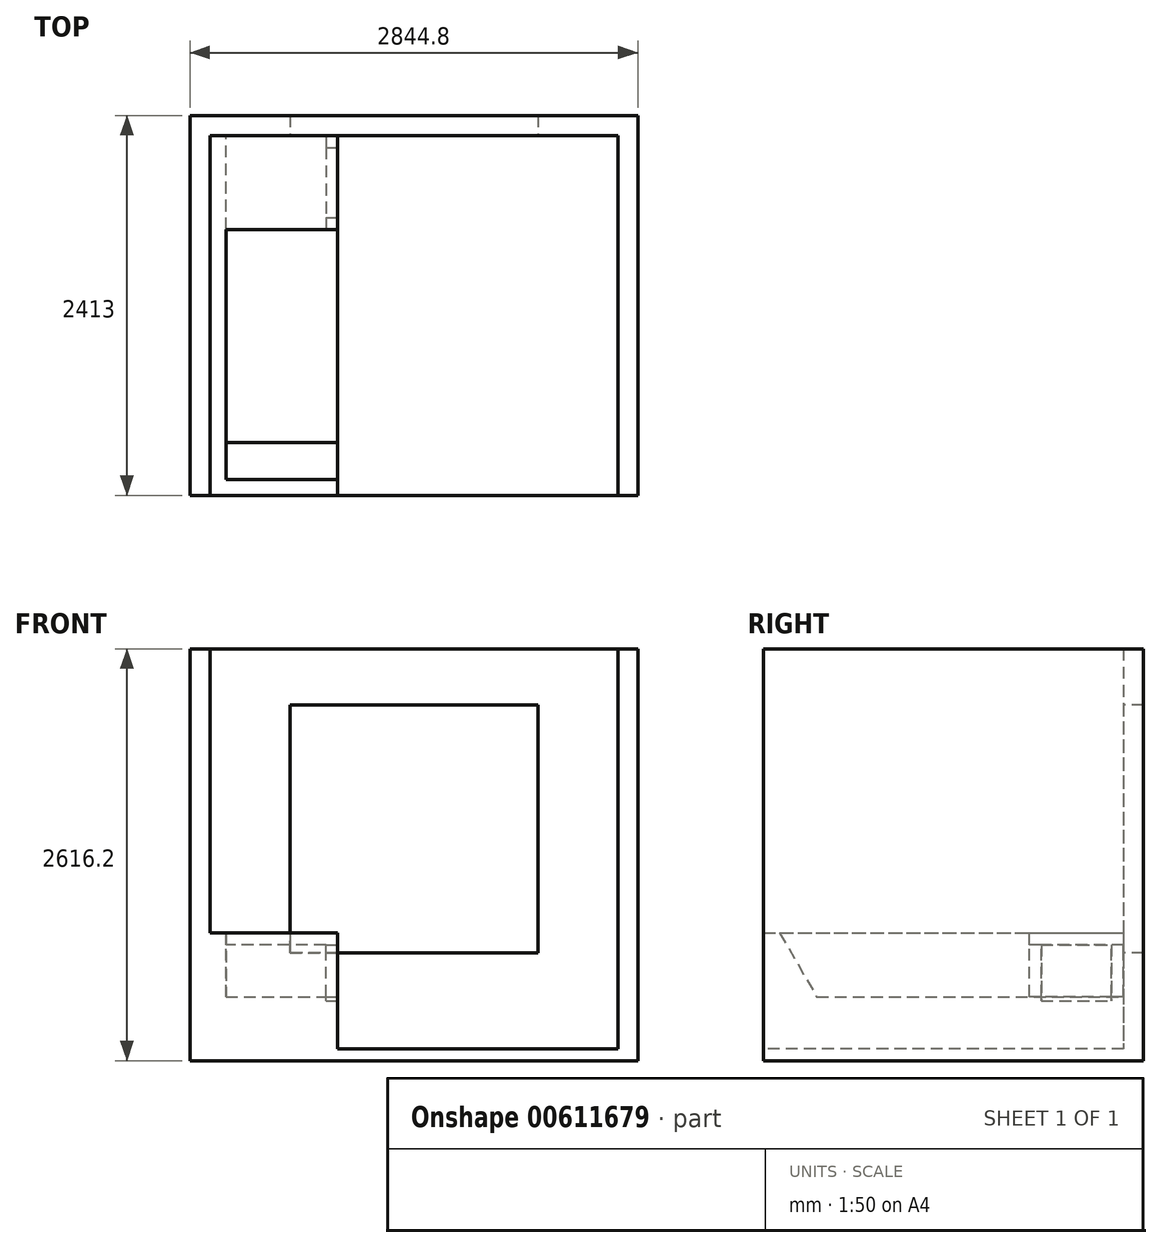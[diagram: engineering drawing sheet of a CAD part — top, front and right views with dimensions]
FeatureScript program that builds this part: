
annotation { "Feature Type Name" : "Feature", "Feature Type Description" : "" }
export const myFeature = defineFeature(function(context is Context, id is Id, definition is map)
    precondition{}
    {
        {
            var Q0;
            Q0=qCreatedBy(makeId("Top.planeOp"),FACE);
            var sketch = newSketch(context, id + "F0", { "sketchPlane" : qUnion([Q0])});
            skLineSegment(sketch, "E0.bottom", {"start": v(-1445.03, 789.88) * mm, "end": v(1145.77, 789.88) * mm});
            skLineSegment(sketch, "E0.left", {"start": v(-1445.03, 789.88) * mm, "end": v(-1445.03, -1496.12) * mm});
            skLineSegment(sketch, "E0.right", {"start": v(1145.77, 789.88) * mm, "end": v(1145.77, -1496.12) * mm});
            skLineSegment(sketch, "E1.0", {"start": v(-1572.03, 916.88) * mm, "end": v(-1572.03, -1496.12) * mm});
            skLineSegment(sketch, "E1.1", {"start": v(-1572.03, 916.88) * mm, "end": v(1272.77, 916.88) * mm});
            skLineSegment(sketch, "E1.2", {"start": v(1272.77, 916.88) * mm, "end": v(1272.77, -1496.12) * mm});
            skLineSegment(sketch, "E2", {"start": v(-1445.03, -1496.12) * mm, "end": v(-1572.03, -1496.12) * mm});
            skLineSegment(sketch, "E3", {"start": v(1145.77, -1496.12) * mm, "end": v(1272.77, -1496.12) * mm});
            skSolve(sketch);
        }
        {
            var Q0;
            Q0 = qSketchRegion(id + "F0", true);
            extrude(context, id + "F1", {"entities" : qUnion([Q0]), "depth" : 2540 * mm, "offsetDistance" : 25.4 * mm});
        }
        {
            var Q0;
            Q0=makeQuery(id+"F1.opExtrude","CAP_FACE",FACE,{"disambiguationData":[OSD([sQuery(id+"F0.wireOp",EDGE,"E0.bottom"),sQuery(id+"F0.wireOp",EDGE,"E0.left"),sQuery(id+"F0.wireOp",EDGE,"E0.right"),sQuery(id+"F0.wireOp",EDGE,"E1.0"),sQuery(id+"F0.wireOp",EDGE,"E1.1"),sQuery(id+"F0.wireOp",EDGE,"E1.2"),sQuery(id+"F0.wireOp",EDGE,"E2"),sQuery(id+"F0.wireOp",EDGE,"E3")])],"isStart":true});
            var sketch = newSketch(context, id + "F2", { "sketchPlane" : qUnion([Q0])});
            skLineSegment(sketch, "E4.bottom", {"start": v(-1572.03, 1496.12) * mm, "end": v(1272.77, 1496.12) * mm});
            skLineSegment(sketch, "E4.top", {"start": v(-1572.03, -916.88) * mm, "end": v(1272.77, -916.88) * mm});
            skLineSegment(sketch, "E4.left", {"start": v(-1572.03, 1496.12) * mm, "end": v(-1572.03, -916.88) * mm});
            skLineSegment(sketch, "E4.right", {"start": v(1272.77, 1496.12) * mm, "end": v(1272.77, -916.88) * mm});
            skSolve(sketch);
        }
        {
            var Q0;
            Q0 = qSketchRegion(id + "F2", true);
            extrude(context, id + "F3", {"entities" : qUnion([Q0]), "operationType" : NewBodyOperationType.ADD, "depth" : 76.2 * mm, "offsetDistance" : 25.4 * mm});
        }
        {
            var Q0;
            Q0=makeQuery(id+"F1.opExtrude","SWEPT_FACE",FACE,{"disambiguationData":[OSD([sQuery(id+"F0.wireOp",EDGE,"E0.bottom")])]});
            var sketch = newSketch(context, id + "F4", { "sketchPlane" : qUnion([Q0])});
            skLineSegment(sketch, "E5.bottom", {"start": v(-937.03, 2184.4) * mm, "end": v(637.77, 2184.4) * mm});
            skLineSegment(sketch, "E5.top", {"start": v(-937.03, 609.6) * mm, "end": v(637.77, 609.6) * mm});
            skLineSegment(sketch, "E5.left", {"start": v(-937.03, 2184.4) * mm, "end": v(-937.03, 609.6) * mm});
            skLineSegment(sketch, "E5.right", {"start": v(637.77, 2184.4) * mm, "end": v(637.77, 609.6) * mm});
            skLineSegment(sketch, "E6", {"start": v(-149.63, 2184.4) * mm, "end": v(-149.63, 609.6) * mm, "construction": true});
            skLineSegment(sketch, "E7", {"start": v(-149.63, 2540) * mm, "end": v(-149.63, 0) * mm, "construction": true});
            skSolve(sketch);
        }
        {
            var Q0;
            Q0 = qSketchRegion(id + "F4", true);
            extrude(context, id + "F5", {"entities" : qUnion([Q0]), "operationType" : NewBodyOperationType.REMOVE, "endBound" : BoundingType.THROUGH_ALL, "oppositeDirection" : true, "depth" : 25.4 * mm, "offsetDistance" : 25.4 * mm});
        }
        {
            var Q0;
            Q0=makeQuery(id+"F1.opExtrude","SWEPT_FACE",FACE,{"disambiguationData":[OSD([sQuery(id+"F0.wireOp",EDGE,"E0.left")])]});
            var sketch = newSketch(context, id + "F6", { "sketchPlane" : qUnion([Q0])});
            skLineSegment(sketch, "E8.bottom", {"start": v(-1496.12, 736.6) * mm, "end": v(789.88, 736.6) * mm});
            skLineSegment(sketch, "E8.top", {"start": v(-1496.12, 0) * mm, "end": v(789.88, 0) * mm});
            skLineSegment(sketch, "E8.left", {"start": v(-1496.12, 736.6) * mm, "end": v(-1496.12, 0) * mm});
            skLineSegment(sketch, "E8.right", {"start": v(789.88, 736.6) * mm, "end": v(789.88, 0) * mm});
            skSolve(sketch);
        }
        {
            var Q0;
            Q0 = qSketchRegion(id + "F6", true);
            extrude(context, id + "F7", {"entities" : qUnion([Q0]), "operationType" : NewBodyOperationType.ADD, "depth" : 812.8 * mm, "offsetDistance" : 25.4 * mm});
        }
        {
            var Q0;
            Q0=makeQuery(id+"F7.opExtrude","CAP_FACE",FACE,{"disambiguationData":[OSD([sQuery(id+"F6.wireOp",EDGE,"E8.bottom"),sQuery(id+"F6.wireOp",EDGE,"E8.top"),sQuery(id+"F6.wireOp",EDGE,"E8.left"),sQuery(id+"F6.wireOp",EDGE,"E8.right")])],"isStart":false});
            var sketch = newSketch(context, id + "F8", { "sketchPlane" : qUnion([Q0])});
            skLineSegment(sketch, "E9", {"start": v(-1394.52, 736.6) * mm, "end": v(-1159.89, 330.2) * mm});
            skLineSegment(sketch, "E10", {"start": v(-1159.89, 330.2) * mm, "end": v(191.02, 330.2) * mm});
            skLineSegment(sketch, "E11", {"start": v(191.02, 330.2) * mm, "end": v(191.02, 736.6) * mm});
            skLineSegment(sketch, "E12", {"start": v(191.02, 736.6) * mm, "end": v(-1394.52, 736.6) * mm});
            skSolve(sketch);
        }
        {
            var Q0;
            Q0=makeQuery(id+"F8.imprint","IMPRINT",FACE,{"disambiguationData":[TD([[makeQuery(id+"F8.imprint","IMPRINT",EDGE,{"derivedFrom":sQuery(id+"F8.wireOp",EDGE,"E9")}),1.0]])]});
            extrude(context, id + "F9", {"entities" : qUnion([Q0]), "operationType" : NewBodyOperationType.REMOVE, "oppositeDirection" : true, "depth" : 711.2 * mm, "offsetDistance" : 25.4 * mm});
        }
        {
            var Q0;
            Q0=makeQuery(id+"F9.boolean.opBoolean","COPY",FACE,{"derivedFrom":makeQuery(id+"F9.opExtrude","SWEPT_FACE",FACE,{"disambiguationData":[OSD([sQuery(id+"F8.wireOp",EDGE,"E11")])]})});
            var sketch = newSketch(context, id + "F10", { "sketchPlane" : qUnion([Q0])});
            skLineSegment(sketch, "E13.bottom", {"start": v(-708.43, 330.2) * mm, "end": v(-1343.43, 330.2) * mm});
            skLineSegment(sketch, "E13.top", {"start": v(-708.43, 660.4) * mm, "end": v(-1343.43, 660.4) * mm});
            skLineSegment(sketch, "E13.left", {"start": v(-708.43, 330.2) * mm, "end": v(-708.43, 660.4) * mm});
            skLineSegment(sketch, "E13.right", {"start": v(-1343.43, 330.2) * mm, "end": v(-1343.43, 660.4) * mm});
            skSolve(sketch);
        }
        {
            var Q0;
            Q0=makeQuery(id+"F10.imprint","IMPRINT",FACE,{"disambiguationData":[TD([[makeQuery(id+"F10.imprint","IMPRINT",EDGE,{"derivedFrom":sQuery(id+"F10.wireOp",EDGE,"E13.bottom")}),1.0]])]});
            var Q1;
            Q1=makeQuery(id+"F1.opExtrude","SWEPT_FACE",FACE,{"disambiguationData":[OSD([sQuery(id+"F0.wireOp",EDGE,"E0.bottom")])]});
            extrude(context, id + "F11", {"entities" : qUnion([Q0]), "operationType" : NewBodyOperationType.REMOVE, "endBound" : BoundingType.UP_TO_SURFACE, "oppositeDirection" : true, "depth" : 25.4 * mm, "endBoundEntityFace" : qUnion([Q1]), "offsetDistance" : 25.4 * mm});
        }
        {
            var Q0;
            Q0=makeQuery(id+"F7.opExtrude","CAP_FACE",FACE,{"disambiguationData":[OSD([sQuery(id+"F6.wireOp",EDGE,"E8.bottom"),sQuery(id+"F6.wireOp",EDGE,"E8.top"),sQuery(id+"F6.wireOp",EDGE,"E8.left"),sQuery(id+"F6.wireOp",EDGE,"E8.right")])],"isStart":false});
            var sketch = newSketch(context, id + "F12", { "sketchPlane" : qUnion([Q0])});
            skLineSegment(sketch, "E14.bottom", {"start": v(267.22, 660.4) * mm, "end": v(713.68, 660.4) * mm});
            skLineSegment(sketch, "E14.top", {"start": v(267.22, 304.8) * mm, "end": v(713.68, 304.8) * mm});
            skLineSegment(sketch, "E14.left", {"start": v(267.22, 660.4) * mm, "end": v(267.22, 304.8) * mm});
            skLineSegment(sketch, "E14.right", {"start": v(713.68, 660.4) * mm, "end": v(713.68, 304.8) * mm});
            skSolve(sketch);
        }
        {
            var Q0;
            Q0=makeQuery(id+"F12.imprint","IMPRINT",FACE,{"disambiguationData":[TD([[makeQuery(id+"F12.imprint","IMPRINT",EDGE,{"derivedFrom":sQuery(id+"F12.wireOp",EDGE,"E14.bottom")}),-1.0]])]});
            var Q1;
            Q1=makeQuery(id+"F11.boolean.opBoolean","COPY",FACE,{"derivedFrom":makeQuery(id+"F11.opExtrude","SWEPT_FACE",FACE,{"disambiguationData":[OSD([sQuery(id+"F10.wireOp",EDGE,"E13.left")])]})});
            extrude(context, id + "F13", {"entities" : qUnion([Q0]), "operationType" : NewBodyOperationType.REMOVE, "endBound" : BoundingType.UP_TO_SURFACE, "oppositeDirection" : true, "depth" : 25.4 * mm, "endBoundEntityFace" : qUnion([Q1]), "offsetDistance" : 25.4 * mm});
        }
    });
